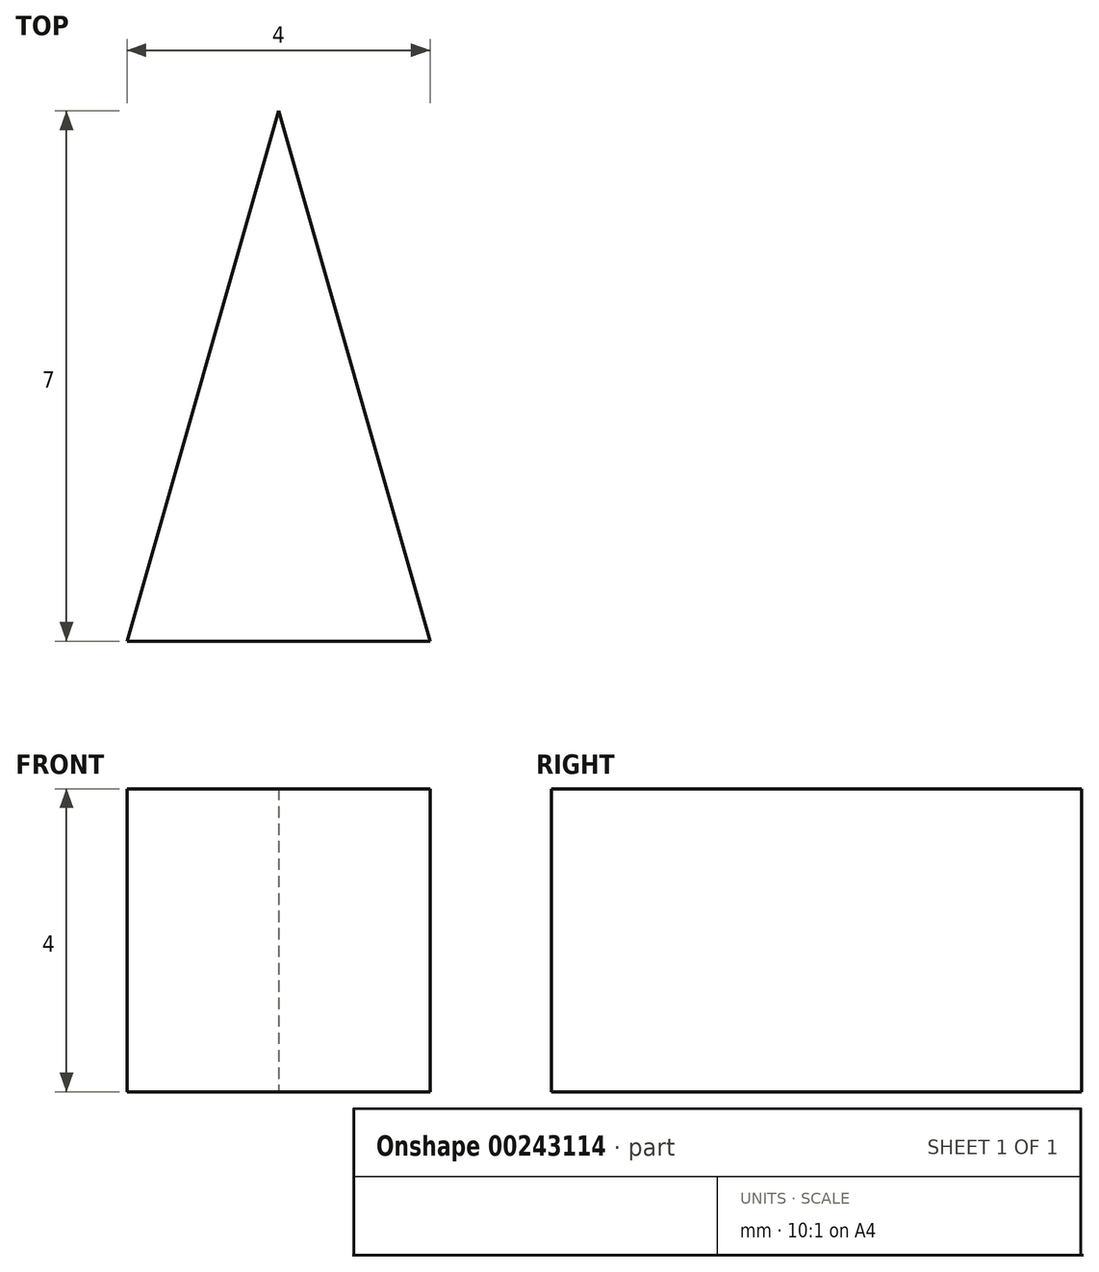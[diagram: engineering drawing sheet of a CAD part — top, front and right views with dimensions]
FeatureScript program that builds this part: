
annotation { "Feature Type Name" : "Feature", "Feature Type Description" : "" }
export const myFeature = defineFeature(function(context is Context, id is Id, definition is map)
    precondition{}
    {
        {
            var Q0;
            Q0=qCreatedBy(makeId("Top.planeOp"),FACE);
            var sketch = newSketch(context, id + "F0", { "sketchPlane" : qUnion([Q0])});
            skLineSegment(sketch, "E0", {"start": v(0, 0) * mm, "end": v(4, 0) * mm});
            skLineSegment(sketch, "E1", {"start": v(4, 0) * mm, "end": v(4, 7) * mm});
            skLineSegment(sketch, "E2", {"start": v(4, 7) * mm, "end": v(0, 7) * mm});
            skLineSegment(sketch, "E3", {"start": v(0, 7) * mm, "end": v(0, 0) * mm});
            skSolve(sketch);
        }
        {
            var Q0;
            Q0 = qSketchRegion(id + "F0", true);
            extrude(context, id + "F1", {"entities" : qUnion([Q0]), "depth" : 4 * mm});
        }
        {
            var Q0;
            Q0=makeQuery(id+"F1.opExtrude","SWEPT_FACE",FACE,{"disambiguationData":[OSD([sQuery(id+"F0.wireOp",EDGE,"E2")])]});
            var sketch = newSketch(context, id + "F2", { "sketchPlane" : qUnion([Q0])});
            skLineSegment(sketch, "E4", {"start": v(0, 0) * mm, "end": v(-4, 4) * mm});
            skLineSegment(sketch, "E5", {"start": v(-4, 0) * mm, "end": v(0, 4) * mm});
            skSolve(sketch);
        }
        {
            var Q0;
            Q0=sQuery(id+"F2.wireOp",EDGE,"E5");
            cPoint(context, id + "F3", {"entities" : qUnion([Q0]), "parameter" : 0.5});
        }
        {
            var Q0;
            Q0 = qCreatedBy(id + "F3" ,VERTEX);
            var Q1;
            Q1=makeQuery(id+"F1.opExtrude","CAP_VERTEX",VERTEX,{"disambiguationData":[OSD([sQuery(id+"F0.wireOp",EDGE,"E0"),sQuery(id+"F0.wireOp",EDGE,"E1")])],"isStart":false});
            var Q2;
            Q2=makeQuery(id+"F1.opExtrude","CAP_VERTEX",VERTEX,{"disambiguationData":[OSD([sQuery(id+"F0.wireOp",EDGE,"E0"),sQuery(id+"F0.wireOp",EDGE,"E1")])],"isStart":true});
            cPlane(context, id + "F4", {"entities" : qUnion([Q0, Q1, Q2]), "cplaneType" : CPlaneType.THREE_POINT, "offset" : 25 * mm, "width" : 150 * mm, "height" : 150 * mm});
        }
        {
            var Q0;
            Q0=qCreatedBy(id+"F4.planeOp",FACE);
            var sketch = newSketch(context, id + "F5", { "sketchPlane" : qUnion([Q0])});
            skLineSegment(sketch, "E6", {"start": v(7.06, 9.72) * mm, "end": v(-14.32, 4.8) * mm});
            skLineSegment(sketch, "E7", {"start": v(-14.32, 4.8) * mm, "end": v(-11.36, -8.08) * mm});
            skLineSegment(sketch, "E8", {"start": v(-11.36, -8.08) * mm, "end": v(9.26, -3.33) * mm});
            skLineSegment(sketch, "E9", {"start": v(9.26, -3.33) * mm, "end": v(7.06, 9.72) * mm});
            skSolve(sketch);
        }
        {
            var Q0;
            Q0 = qSketchRegion(id + "F5", true);
            extrude(context, id + "F6", {"entities" : qUnion([Q0]), "operationType" : NewBodyOperationType.REMOVE, "oppositeDirection" : true, "depth" : 25 * mm});
        }
        {
            var Q0;
            Q0=sQuery(id+"F2.wireOp",EDGE,"E5");
            cPoint(context, id + "F7", {"entities" : qUnion([Q0]), "parameter" : 0.5});
        }
        {
            var Q0;
            Q0 = qCreatedBy(id + "F7" ,VERTEX);
            var Q1;
            Q1=makeQuery(id+"F1.opExtrude","CAP_VERTEX",VERTEX,{"disambiguationData":[OSD([sQuery(id+"F0.wireOp",EDGE,"E0"),sQuery(id+"F0.wireOp",EDGE,"E3")])],"isStart":false});
            var Q2;
            Q2=qCreatedBy(makeId("Origin.pointOp"),VERTEX);
            cPlane(context, id + "F8", {"entities" : qUnion([Q0, Q1, Q2]), "cplaneType" : CPlaneType.THREE_POINT, "offset" : 25 * mm, "width" : 150 * mm, "height" : 150 * mm});
        }
        {
            var Q0;
            Q0=qCreatedBy(id+"F8.planeOp",FACE);
            var sketch = newSketch(context, id + "F9", { "sketchPlane" : qUnion([Q0])});
            skLineSegment(sketch, "E10", {"start": v(-6.77, -9.41) * mm, "end": v(6.3, -9.41) * mm});
            skLineSegment(sketch, "E11", {"start": v(6.3, -9.41) * mm, "end": v(3.88, 17.09) * mm});
            skLineSegment(sketch, "E12", {"start": v(3.88, 17.09) * mm, "end": v(-6.92, 14.66) * mm});
            skLineSegment(sketch, "E13", {"start": v(-6.92, 14.66) * mm, "end": v(-10.43, 17.94) * mm});
            skLineSegment(sketch, "E14", {"start": v(-10.43, 17.94) * mm, "end": v(-10.43, -10) * mm});
            skLineSegment(sketch, "E15", {"start": v(-10.43, -10) * mm, "end": v(-6.77, -9.41) * mm});
            skSolve(sketch);
        }
        {
            var Q0;
            Q0 = qSketchRegion(id + "F9", true);
            extrude(context, id + "F10", {"entities" : qUnion([Q0]), "operationType" : NewBodyOperationType.REMOVE, "depth" : 25 * mm});
        }
    });
